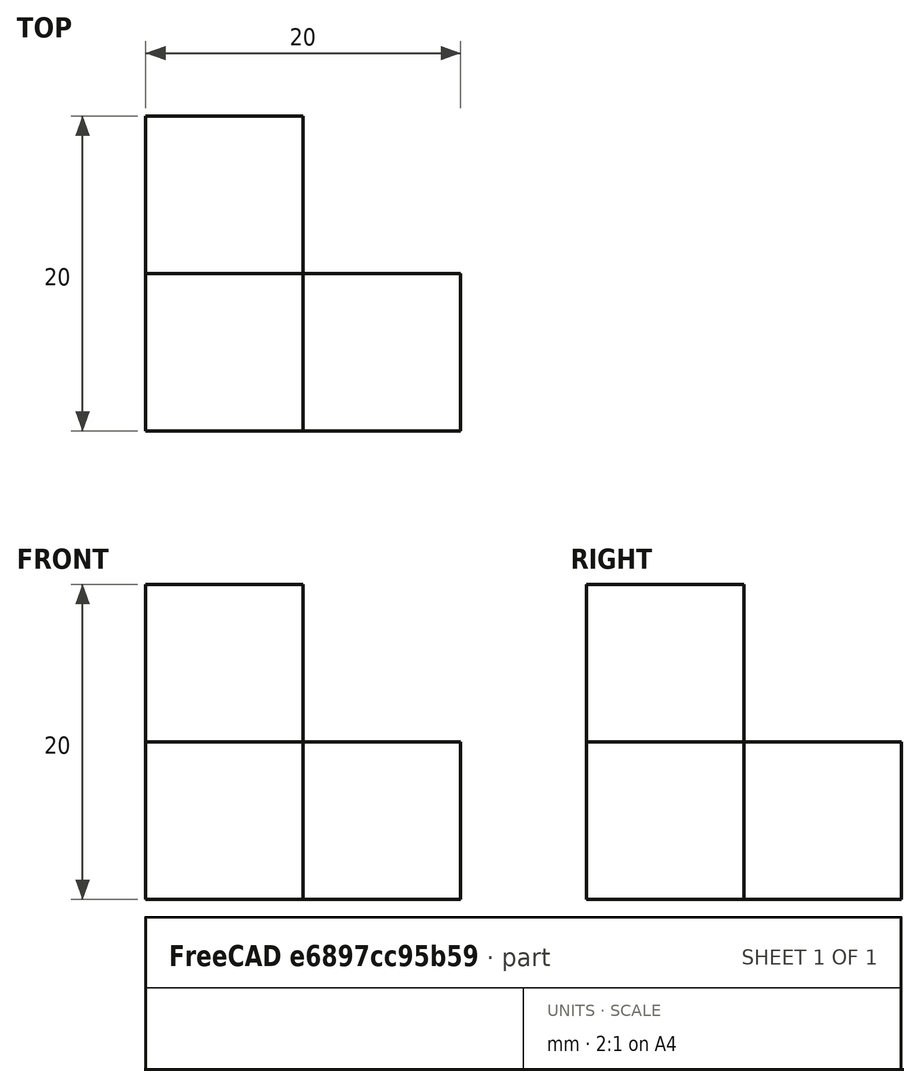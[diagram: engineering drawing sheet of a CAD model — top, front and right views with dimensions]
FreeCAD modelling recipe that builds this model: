
FCSTD DOCUMENT  (FreeCAD 0.21R33771 (Git))
Label: OJT1_T04P01_qbert2nivells_v2
License: All rights reserved
LicenseURL: http://en.wikipedia.org/wiki/All_rights_reserved
objects: Part::Box×4
note: 4 computed .brp shape members not serialized (recipe doc carries the construction recipe); baked Part::Feature solids carry a one-line shape summary decoded from their .brp

FEATURE [Part::Box] Box  label="nivell1_cub1"
  AttacherType = Attacher::AttachEngine3D
  Height = 10
  Length = 10
  Width = 10
FEATURE [Part::Box] Box001  label="nivell2_cub1"
  AttacherType = Attacher::AttachEngine3D
  Height = 10
  Length = 10
  Placement = pos=(0,10,0) rot=(0,0,1;0rad)
  Width = 10
FEATURE [Part::Box] Box002  label="nivell2_cub2"
  AttacherType = Attacher::AttachEngine3D
  Height = 10
  Length = 10
  Placement = pos=(10,0,0) rot=(0,0,1;0rad)
  Width = 10
FEATURE [Part::Box] Box003  label="nivell1_cub2"
  AttacherType = Attacher::AttachEngine3D
  Height = 10
  Length = 10
  Placement = pos=(0,0,10) rot=(0,0,1;0rad)
  Width = 10
